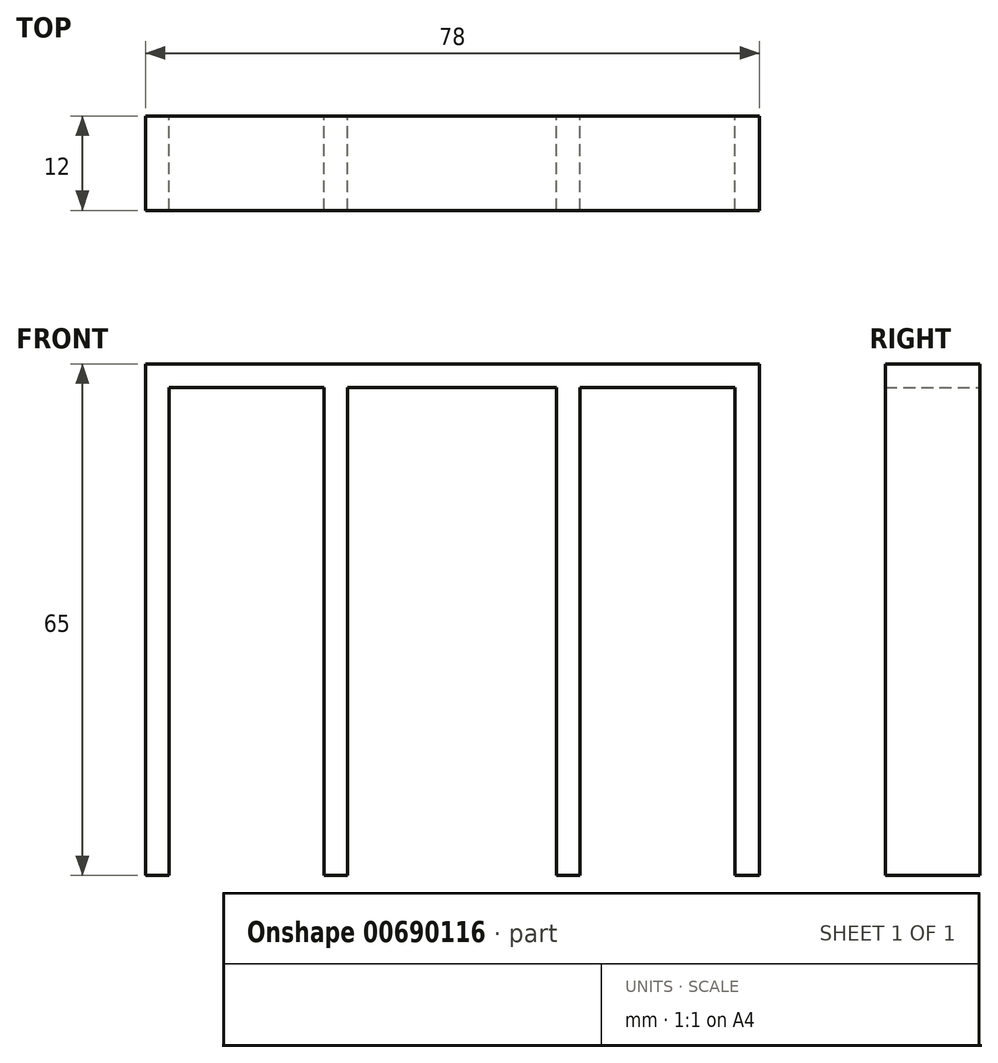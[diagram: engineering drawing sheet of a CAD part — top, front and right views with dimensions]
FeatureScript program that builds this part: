
annotation { "Feature Type Name" : "Feature", "Feature Type Description" : "" }
export const myFeature = defineFeature(function(context is Context, id is Id, definition is map)
    precondition{}
    {
        {
            var Q0;
            Q0=qCreatedBy(makeId("Front.planeOp"),FACE);
            var sketch = newSketch(context, id + "F0", { "sketchPlane" : qUnion([Q0])});
            skLineSegment(sketch, "E0", {"start": v(0, 0) * mm, "end": v(0, 65) * mm});
            skLineSegment(sketch, "E1", {"start": v(0, 65) * mm, "end": v(78, 65) * mm});
            skLineSegment(sketch, "E2", {"start": v(78, 65) * mm, "end": v(78, 0) * mm});
            skLineSegment(sketch, "E3", {"start": v(78, 0) * mm, "end": v(74.9, 0) * mm});
            skLineSegment(sketch, "E4", {"start": v(74.9, 0) * mm, "end": v(74.9, 62) * mm});
            skLineSegment(sketch, "E5", {"start": v(74.9, 62) * mm, "end": v(55.2, 62) * mm});
            skLineSegment(sketch, "E6", {"start": v(55.2, 62) * mm, "end": v(55.2, 0) * mm});
            skLineSegment(sketch, "E7", {"start": v(55.2, 0) * mm, "end": v(52.2, 0) * mm});
            skLineSegment(sketch, "E8", {"start": v(52.2, 0) * mm, "end": v(52.2, 62) * mm});
            skLineSegment(sketch, "E9", {"start": v(52.2, 62) * mm, "end": v(25.7, 62) * mm});
            skLineSegment(sketch, "E10", {"start": v(25.7, 62) * mm, "end": v(25.7, 0) * mm});
            skLineSegment(sketch, "E11", {"start": v(25.7, 0) * mm, "end": v(22.7, 0) * mm});
            skLineSegment(sketch, "E12", {"start": v(22.7, 0) * mm, "end": v(22.7, 62) * mm});
            skLineSegment(sketch, "E13", {"start": v(22.7, 62) * mm, "end": v(3, 62) * mm});
            skLineSegment(sketch, "E14", {"start": v(3, 62) * mm, "end": v(3, 0) * mm});
            skLineSegment(sketch, "E15", {"start": v(3, 0) * mm, "end": v(0, 0) * mm});
            skSolve(sketch);
        }
        {
            var Q0;
            Q0=makeQuery(id+"F0.imprint","IMPRINT",FACE,{"disambiguationData":[TD([[makeQuery(id+"F0.imprint","IMPRINT",EDGE,{"derivedFrom":sQuery(id+"F0.wireOp",EDGE,"E0")}),-1.0]])]});
            extrude(context, id + "F1", {"entities" : qUnion([Q0]), "depth" : 12 * mm, "offsetDistance" : 25.4 * mm});
        }
    });
